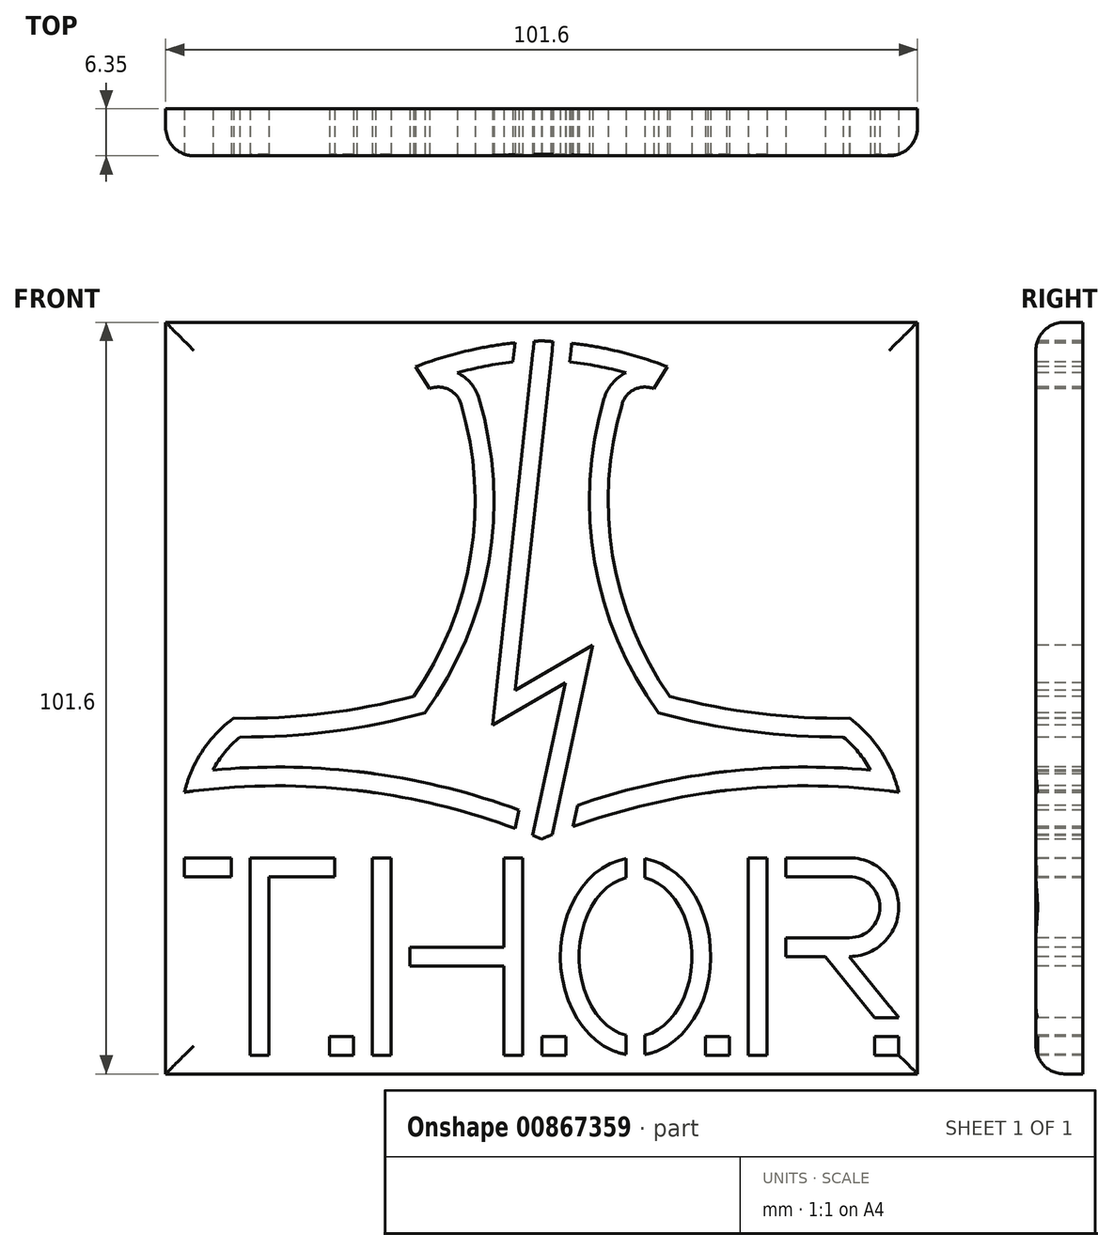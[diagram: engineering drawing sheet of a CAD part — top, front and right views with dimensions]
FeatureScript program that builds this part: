
annotation { "Feature Type Name" : "Feature", "Feature Type Description" : "" }
export const myFeature = defineFeature(function(context is Context, id is Id, definition is map)
    precondition{}
    {
        {
            var Q0;
            Q0=qCreatedBy(makeId("Front.planeOp"),FACE);
            var sketch = newSketch(context, id + "F0", { "sketchPlane" : qUnion([Q0])});
            skLineSegment(sketch, "E0.bottom", {"start": v(50.8, 50.8) * mm, "end": v(-50.8, 50.8) * mm});
            skLineSegment(sketch, "E0.top", {"start": v(50.8, -50.8) * mm, "end": v(-50.8, -50.8) * mm});
            skLineSegment(sketch, "E0.left", {"start": v(50.8, 50.8) * mm, "end": v(50.8, -50.8) * mm});
            skLineSegment(sketch, "E0.right", {"start": v(-50.8, 50.8) * mm, "end": v(-50.8, -50.8) * mm});
            skPoint(sketch, "E0.middle", {"position": v(0, 0) * mm});
            skSolve(sketch);
        }
        {
            var Q0;
            Q0 = qSketchRegion(id + "F0", true);
            extrude(context, id + "F1", {"entities" : qUnion([Q0]), "depth" : 6.35 * mm, "offsetDistance" : 25.4 * mm});
        }
        {
            var Q0;
            Q0=makeQuery(id+"F1.opExtrude","CAP_FACE",FACE,{"disambiguationData":[OSD([sQuery(id+"F0.wireOp",EDGE,"E0.bottom"),sQuery(id+"F0.wireOp",EDGE,"E0.top"),sQuery(id+"F0.wireOp",EDGE,"E0.left"),sQuery(id+"F0.wireOp",EDGE,"E0.right")])],"isStart":false});
            var sketch = newSketch(context, id + "F2", { "sketchPlane" : qUnion([Q0])});
            skLineSegment(sketch, "E1", {"start": v(-25.4, 50.8) * mm, "end": v(-25.4, -50.8) * mm, "construction": true});
            skLineSegment(sketch, "E2", {"start": v(0, 50.8) * mm, "end": v(0, -50.8) * mm, "construction": true});
            skLineSegment(sketch, "E3", {"start": v(25.4, 50.8) * mm, "end": v(25.4, -50.8) * mm, "construction": true});
            skLineSegment(sketch, "E4", {"start": v(-50.8, 0) * mm, "end": v(50.8, 0) * mm, "construction": true});
            skLineSegment(sketch, "E5", {"start": v(-50.8, 25.4) * mm, "end": v(50.8, 25.4) * mm, "construction": true});
            skLineSegment(sketch, "E6", {"start": v(-50.8, -21.6) * mm, "end": v(-41.91, -21.6) * mm, "construction": true});
            skLineSegment(sketch, "E7.bottom", {"start": v(-48.26, -21.6) * mm, "end": v(-41.91, -21.6) * mm});
            skLineSegment(sketch, "E7.top", {"start": v(-48.26, -24.13) * mm, "end": v(-41.91, -24.13) * mm});
            skLineSegment(sketch, "E7.left", {"start": v(-48.26, -21.6) * mm, "end": v(-48.26, -24.13) * mm});
            skLineSegment(sketch, "E7.right", {"start": v(-27.94, -21.6) * mm, "end": v(-27.94, -24.13) * mm});
            skLineSegment(sketch, "E8.top", {"start": v(-39.37, -48.26) * mm, "end": v(-36.83, -48.26) * mm});
            skLineSegment(sketch, "E8.left", {"start": v(-39.37, -24.13) * mm, "end": v(-39.37, -48.26) * mm});
            skLineSegment(sketch, "E8.right", {"start": v(-36.83, -24.13) * mm, "end": v(-36.83, -48.26) * mm});
            skLineSegment(sketch, "E9", {"start": v(-38.1, -21.6) * mm, "end": v(-38.1, -50.8) * mm, "construction": true});
            skLineSegment(sketch, "E10.trimOffspring", {"start": v(-36.83, -24.13) * mm, "end": v(-27.94, -24.13) * mm});
            skLineSegment(sketch, "E11.bottom", {"start": v(-22.86, -21.6) * mm, "end": v(-20.32, -21.6) * mm});
            skLineSegment(sketch, "E11.top", {"start": v(-22.86, -48.26) * mm, "end": v(-20.32, -48.26) * mm});
            skLineSegment(sketch, "E11.left", {"start": v(-22.86, -21.6) * mm, "end": v(-22.86, -48.26) * mm});
            skLineSegment(sketch, "E11.right", {"start": v(-20.32, -21.6) * mm, "end": v(-20.32, -33.66) * mm});
            skLineSegment(sketch, "E12.bottom", {"start": v(-5.08, -21.6) * mm, "end": v(-2.54, -21.6) * mm});
            skLineSegment(sketch, "E12.top", {"start": v(-5.08, -48.26) * mm, "end": v(-2.54, -48.26) * mm});
            skLineSegment(sketch, "E12.left", {"start": v(-5.08, -21.6) * mm, "end": v(-5.08, -33.66) * mm});
            skLineSegment(sketch, "E12.right", {"start": v(-2.54, -21.59) * mm, "end": v(-2.54, -48.26) * mm});
            skLineSegment(sketch, "E13.bottom", {"start": v(-17.78, -33.66) * mm, "end": v(-5.08, -33.66) * mm});
            skLineSegment(sketch, "E13.top", {"start": v(-17.78, -36.2) * mm, "end": v(-5.08, -36.2) * mm});
            skLineSegment(sketch, "E14", {"start": v(-22.86, -34.93) * mm, "end": v(-2.54, -34.93) * mm, "construction": true});
            skLineSegment(sketch, "E15.trimOffspring", {"start": v(-20.32, -36.2) * mm, "end": v(-20.32, -48.26) * mm});
            skLineSegment(sketch, "E16.trimOffspring", {"start": v(-5.08, -36.2) * mm, "end": v(-5.08, -48.26) * mm});
            skLineSegment(sketch, "E17", {"start": v(-2.54, -34.93) * mm, "end": v(25.4, -34.93) * mm, "construction": true});
            skLineSegment(sketch, "E18", {"start": v(12.7, -50.8) * mm, "end": v(12.7, -21.6) * mm, "construction": true});
            skLineSegment(sketch, "E19", {"start": v(2.54, -21.6) * mm, "end": v(2.54, -50.8) * mm, "construction": true});
            skEllipticalArc(sketch, "E20", {});
            skLineSegment(sketch, "E21", {"start": v(-2.54, -48.26) * mm, "end": v(25.4, -48.26) * mm, "construction": true});
            skLineSegment(sketch, "E22", {"start": v(22.86, -48.26) * mm, "end": v(22.86, -21.6) * mm, "construction": true});
            skEllipticalArc(sketch, "E23", {});
            skLineSegment(sketch, "E24.bottom", {"start": v(27.94, -21.59) * mm, "end": v(30.48, -21.59) * mm});
            skLineSegment(sketch, "E24.top", {"start": v(27.94, -48.26) * mm, "end": v(30.48, -48.26) * mm});
            skLineSegment(sketch, "E24.left", {"start": v(27.94, -21.59) * mm, "end": v(27.94, -48.26) * mm});
            skLineSegment(sketch, "E24.right", {"start": v(30.48, -24.13) * mm, "end": v(30.48, -32.39) * mm});
            skArc(sketch, "E25", {"start": v(41.6, -34.93) * mm, "mid": v(48.26, -28.26) * mm, "end": v(41.6, -21.59) * mm});
            skLineSegment(sketch, "E26", {"start": v(48.26, -21.59) * mm, "end": v(48.26, -50.8) * mm, "construction": true});
            skLineSegment(sketch, "E27", {"start": v(25.4, -34.93) * mm, "end": v(30.48, -34.93) * mm, "construction": true});
            skLineSegment(sketch, "E28.bottom", {"start": v(33.02, -21.59) * mm, "end": v(41.6, -21.59) * mm});
            skLineSegment(sketch, "E28.top", {"start": v(33.02, -24.13) * mm, "end": v(41.6, -24.13) * mm});
            skLineSegment(sketch, "E29.bottom", {"start": v(33.02, -34.93) * mm, "end": v(38.33, -34.93) * mm});
            skLineSegment(sketch, "E29.top", {"start": v(33.02, -32.39) * mm, "end": v(41.6, -32.39) * mm});
            skArc(sketch, "E30", {"start": v(41.6, -32.39) * mm, "mid": v(45.72, -28.26) * mm, "end": v(41.6, -24.13) * mm});
            skLineSegment(sketch, "E31.trimOffspring", {"start": v(30.48, -34.93) * mm, "end": v(30.48, -48.26) * mm});
            skLineSegment(sketch, "E32.trimOffspring", {"start": v(41.6, -34.93) * mm, "end": v(48.26, -34.93) * mm, "construction": true});
            skArc(sketch, "E33", {"start": v(48.26, -12.72) * mm, "mid": v(36.62, -11.86) * mm, "end": v(24.97, -12.49) * mm});
            skArc(sketch, "E34", {"start": v(10.88, 39.75) * mm, "mid": v(9.58, 19.25) * mm, "end": v(17.31, 0.22) * mm});
            skArc(sketch, "E35", {"start": v(15.16, 41.8) * mm, "mid": v(12.56, 41.73) * mm, "end": v(10.88, 39.75) * mm});
            skLineSegment(sketch, "E36", {"start": v(15.16, 41.8) * mm, "end": v(17, 44.79) * mm});
            skArc(sketch, "E37", {"start": v(48.26, -12.72) * mm, "mid": v(45.83, -7.14) * mm, "end": v(41.63, -2.72) * mm});
            skArc(sketch, "E38", {"start": v(17.31, 0.22) * mm, "mid": v(29.37, -2.07) * mm, "end": v(41.63, -2.72) * mm});
            skArc(sketch, "E39", {"start": v(17, 44.79) * mm, "mid": v(9.27, 47.12) * mm, "end": v(1.27, 48.2) * mm});
            skArc(sketch, "E40.MirrorCS", {"start": v(-48.26, -12.72) * mm, "mid": v(-36.62, -11.86) * mm, "end": v(-24.97, -12.49) * mm});
            skArc(sketch, "E41.MirrorCS", {"start": v(-48.26, -12.72) * mm, "mid": v(-45.83, -7.14) * mm, "end": v(-41.63, -2.72) * mm});
            skArc(sketch, "E42.MirrorCS", {"start": v(-17.31, 0.22) * mm, "mid": v(-29.37, -2.07) * mm, "end": v(-41.63, -2.72) * mm});
            skArc(sketch, "E43.MirrorCS", {"start": v(-10.88, 39.75) * mm, "mid": v(-9.58, 19.25) * mm, "end": v(-17.31, 0.22) * mm});
            skArc(sketch, "E44.MirrorCS", {"start": v(-15.16, 41.8) * mm, "mid": v(-12.56, 41.73) * mm, "end": v(-10.88, 39.75) * mm});
            skLineSegment(sketch, "E45.MirrorCS", {"start": v(-15.16, 41.8) * mm, "end": v(-17, 44.79) * mm});
            skArc(sketch, "E46.MirrorCS", {"start": v(-17, 44.79) * mm, "mid": v(-9.27, 47.12) * mm, "end": v(-1.27, 48.2) * mm});
            skLineSegment(sketch, "E47", {"start": v(11.43, -24.28) * mm, "end": v(11.43, -21.7) * mm});
            skLineSegment(sketch, "E48", {"start": v(13.97, -24.28) * mm, "end": v(13.97, -21.7) * mm});
            skLineSegment(sketch, "E49", {"start": v(11.43, -48.16) * mm, "end": v(11.43, -45.57) * mm});
            skLineSegment(sketch, "E50", {"start": v(13.97, -45.57) * mm, "end": v(13.97, -48.16) * mm});
            skEllipticalArc(sketch, "E51.trimOffspring", {});
            skEllipticalArc(sketch, "E52.trimOffspring", {});
            skLineSegment(sketch, "E53", {"start": v(30.48, -34.93) * mm, "end": v(30.48, -32.39) * mm});
            skLineSegment(sketch, "E54", {"start": v(33.02, -32.39) * mm, "end": v(33.02, -34.93) * mm});
            skLineSegment(sketch, "E55.trimOffspring", {"start": v(33.02, -34.93) * mm, "end": v(38.33, -34.93) * mm, "construction": true});
            skLineSegment(sketch, "E56", {"start": v(30.48, -24.13) * mm, "end": v(30.48, -21.59) * mm});
            skLineSegment(sketch, "E57", {"start": v(33.02, -21.59) * mm, "end": v(33.02, -24.13) * mm});
            skLineSegment(sketch, "E58.trimOffspring", {"start": v(33.02, -21.59) * mm, "end": v(50.8, -21.59) * mm, "construction": true});
            skLineSegment(sketch, "E59", {"start": v(-20.32, -33.66) * mm, "end": v(-20.32, -36.2) * mm});
            skLineSegment(sketch, "E60", {"start": v(-17.78, -33.66) * mm, "end": v(-17.78, -36.2) * mm});
            skLineSegment(sketch, "E61", {"start": v(-39.37, -24.13) * mm, "end": v(-39.37, -21.6) * mm});
            skLineSegment(sketch, "E62", {"start": v(-41.91, -21.6) * mm, "end": v(-41.91, -24.13) * mm});
            skLineSegment(sketch, "E63.trimOffspring", {"start": v(-39.37, -21.6) * mm, "end": v(30.48, -21.59) * mm, "construction": true});
            skLineSegment(sketch, "E64.trimOffspring", {"start": v(-39.37, -21.6) * mm, "end": v(-27.94, -21.6) * mm});
            skLineSegment(sketch, "E65.bottom", {"start": v(48.26, -48.26) * mm, "end": v(45, -48.26) * mm});
            skLineSegment(sketch, "E65.top", {"start": v(48.26, -45.72) * mm, "end": v(45, -45.72) * mm});
            skLineSegment(sketch, "E65.left", {"start": v(48.26, -48.26) * mm, "end": v(48.26, -45.72) * mm});
            skLineSegment(sketch, "E65.right", {"start": v(45, -48.26) * mm, "end": v(45, -45.72) * mm});
            skLineSegment(sketch, "E66.bottom", {"start": v(25.4, -48.26) * mm, "end": v(22.12, -48.26) * mm});
            skLineSegment(sketch, "E66.top", {"start": v(25.4, -45.72) * mm, "end": v(22.12, -45.72) * mm});
            skLineSegment(sketch, "E66.left", {"start": v(25.4, -48.26) * mm, "end": v(25.4, -45.72) * mm});
            skLineSegment(sketch, "E66.right", {"start": v(22.12, -48.26) * mm, "end": v(22.12, -45.72) * mm});
            skLineSegment(sketch, "E67.bottom", {"start": v(-25.4, -48.26) * mm, "end": v(-28.68, -48.26) * mm});
            skLineSegment(sketch, "E67.top", {"start": v(-25.4, -45.72) * mm, "end": v(-28.68, -45.72) * mm});
            skLineSegment(sketch, "E67.left", {"start": v(-25.4, -48.26) * mm, "end": v(-25.4, -45.72) * mm});
            skLineSegment(sketch, "E67.right", {"start": v(-28.68, -48.26) * mm, "end": v(-28.68, -45.72) * mm});
            skLineSegment(sketch, "E68.bottom", {"start": v(0.02, -48.26) * mm, "end": v(3.3, -48.26) * mm});
            skLineSegment(sketch, "E68.top", {"start": v(0.02, -45.72) * mm, "end": v(3.3, -45.72) * mm});
            skLineSegment(sketch, "E68.left", {"start": v(0.02, -48.26) * mm, "end": v(0.02, -45.72) * mm});
            skLineSegment(sketch, "E68.right", {"start": v(3.3, -48.26) * mm, "end": v(3.3, -45.72) * mm});
            skLineSegment(sketch, "E69", {"start": v(38.33, -34.93) * mm, "end": v(45, -43.18) * mm});
            skLineSegment(sketch, "E70", {"start": v(45, -43.18) * mm, "end": v(48.26, -43.18) * mm});
            skLineSegment(sketch, "E71", {"start": v(48.26, -43.18) * mm, "end": v(41.6, -34.93) * mm});
            skArc(sketch, "E72.0", {"start": v(44.42, -9.72) * mm, "mid": v(34.7, -9.33) * mm, "end": v(24.97, -9.93) * mm});
            skArc(sketch, "E72.1", {"start": v(11.39, 43.98) * mm, "mid": v(6.37, 45.09) * mm, "end": v(1.27, 45.66) * mm});
            skArc(sketch, "E72.2", {"start": v(11.39, 43.98) * mm, "mid": v(9.55, 42.53) * mm, "end": v(8.45, 40.47) * mm});
            skArc(sketch, "E72.3", {"start": v(8.45, 40.47) * mm, "mid": v(7.15, 18.38) * mm, "end": v(15.78, -2) * mm});
            skArc(sketch, "E72.4", {"start": v(15.78, -2) * mm, "mid": v(28.16, -4.47) * mm, "end": v(40.77, -5.27) * mm});
            skArc(sketch, "E72.5", {"start": v(-11.39, 43.98) * mm, "mid": v(-6.37, 45.09) * mm, "end": v(-1.27, 45.66) * mm});
            skArc(sketch, "E72.6", {"start": v(44.42, -9.72) * mm, "mid": v(42.8, -7.32) * mm, "end": v(40.77, -5.27) * mm});
            skArc(sketch, "E72.7", {"start": v(-11.39, 43.98) * mm, "mid": v(-9.55, 42.53) * mm, "end": v(-8.45, 40.47) * mm});
            skArc(sketch, "E72.8", {"start": v(-8.45, 40.47) * mm, "mid": v(-7.15, 18.38) * mm, "end": v(-15.78, -2) * mm});
            skArc(sketch, "E72.9", {"start": v(-15.78, -2) * mm, "mid": v(-28.16, -4.47) * mm, "end": v(-40.77, -5.27) * mm});
            skArc(sketch, "E72.10", {"start": v(-44.42, -9.72) * mm, "mid": v(-42.8, -7.32) * mm, "end": v(-40.77, -5.27) * mm});
            skArc(sketch, "E72.11", {"start": v(-44.42, -9.72) * mm, "mid": v(-34.7, -9.33) * mm, "end": v(-24.97, -9.93) * mm});
            skPoint(sketch, "E73.orphan", {"position": v(0, 48.26) * mm});
            skArc(sketch, "E74.trimOffspring", {"start": v(-22.43, -10.25) * mm, "mid": v(-11.03, -12.59) * mm, "end": v(0, -16.3) * mm});
            skArc(sketch, "E75.trimOffspring", {"start": v(-22.43, -12.82) * mm, "mid": v(-11.02, -15.22) * mm, "end": v(0, -19.05) * mm});
            skArc(sketch, "E76.trimOffspring", {"start": v(22.43, -12.82) * mm, "mid": v(11.02, -15.22) * mm, "end": v(0, -19.05) * mm});
            skArc(sketch, "E77.trimOffspring", {"start": v(22.43, -10.25) * mm, "mid": v(11.03, -12.59) * mm, "end": v(0, -16.3) * mm});
            skArc(sketch, "E78", {"start": v(1.27, 45.66) * mm, "mid": v(0, 45.7) * mm, "end": v(-1.27, 45.66) * mm});
            skArc(sketch, "E79", {"start": v(1.27, 48.2) * mm, "mid": v(0, 48.27) * mm, "end": v(-1.27, 48.2) * mm});
            skArc(sketch, "E80", {"start": v(-22.43, -12.82) * mm, "mid": v(-23.7, -12.62) * mm, "end": v(-24.97, -12.49) * mm});
            skArc(sketch, "E81", {"start": v(-22.43, -10.25) * mm, "mid": v(-23.7, -10.07) * mm, "end": v(-24.97, -9.93) * mm});
            skArc(sketch, "E82.MirrorCS", {"start": v(22.43, -10.25) * mm, "mid": v(23.7, -10.07) * mm, "end": v(24.97, -9.93) * mm});
            skArc(sketch, "E83.MirrorCS", {"start": v(22.43, -12.82) * mm, "mid": v(23.7, -12.62) * mm, "end": v(24.97, -12.49) * mm});
            const initialGuessF2  = {"E20": [0.0127, -0.034925, 0, 1, 0.013335, 0.01016, 0.12532783116806362, 3.016264822421728], "E23": [0.0127, -0.034925, 0, 1, 0.010795, 0.00762, 0.167448079219667, 2.9741445743701163], "E51.trimOffspring": [0.0127, -0.034925, 0, 1, 0.010795, 0.00762, 3.3090407328094815, 6.115737227959899], "E52.trimOffspring": [0.0127, -0.034925, 0, 1, 0.013335, 0.01016, 3.2669204847578577, 6.157857476011521]};
            skSetInitialGuess(sketch, initialGuessF2);
            skSolve(sketch);
        }
        {
            var Q0;
            Q0 = qSketchRegion(id + "F2", true);
            extrude(context, id + "F3", {"entities" : qUnion([Q0]), "operationType" : NewBodyOperationType.REMOVE, "oppositeDirection" : true, "depth" : 25.4 * mm, "offsetDistance" : 25.4 * mm});
        }
        {
            var Q0;
            Q0=makeQuery(id+"F1.opExtrude","CAP_FACE",FACE,{"disambiguationData":[OSD([sQuery(id+"F0.wireOp",EDGE,"E0.bottom"),sQuery(id+"F0.wireOp",EDGE,"E0.top"),sQuery(id+"F0.wireOp",EDGE,"E0.left"),sQuery(id+"F0.wireOp",EDGE,"E0.right")])],"isStart":false});
            var sketch = newSketch(context, id + "F4", { "sketchPlane" : qUnion([Q0])});
            skLineSegment(sketch, "E84", {"start": v(0, -19.05) * mm, "end": v(5.08, 4.6) * mm, "construction": true});
            skLineSegment(sketch, "E85", {"start": v(5.08, 4.6) * mm, "end": v(-5.08, -1.3) * mm, "construction": true});
            skLineSegment(sketch, "E86", {"start": v(-5.08, -1.3) * mm, "end": v(0, 45.7) * mm, "construction": true});
            skLineSegment(sketch, "E87", {"start": v(0, 45.7) * mm, "end": v(0, -19.05) * mm, "construction": true});
            skLineSegment(sketch, "E88.0", {"start": v(-3.55, 1.06) * mm, "end": v(1.26, 45.57) * mm});
            skLineSegment(sketch, "E88.1", {"start": v(6.92, 7.14) * mm, "end": v(-3.55, 1.06) * mm});
            skLineSegment(sketch, "E88.2", {"start": v(1.71, -17.13) * mm, "end": v(6.92, 7.14) * mm});
            skLineSegment(sketch, "E89.0", {"start": v(-6.61, -3.66) * mm, "end": v(-1.26, 45.84) * mm});
            skLineSegment(sketch, "E89.1", {"start": v(3.24, 2.06) * mm, "end": v(-6.61, -3.66) * mm});
            skLineSegment(sketch, "E89.2", {"start": v(-0.76, -16.53) * mm, "end": v(3.24, 2.06) * mm});
            skLineSegment(sketch, "E90", {"start": v(-0.76, -16.53) * mm, "end": v(1.71, -17.13) * mm});
            skLineSegment(sketch, "E91", {"start": v(1.26, 45.57) * mm, "end": v(1.36, 46.43) * mm});
            skLineSegment(sketch, "E92", {"start": v(1.36, 46.43) * mm, "end": v(-1.26, 45.84) * mm});
            skSolve(sketch);
        }
        {
            var Q0;
            Q0 = qSketchRegion(id + "F4", true);
            extrude(context, id + "F5", {"entities" : qUnion([Q0]), "operationType" : NewBodyOperationType.REMOVE, "oppositeDirection" : true, "depth" : 25.4 * mm, "offsetDistance" : 25.4 * mm});
        }
        {
            var Q0;
            Q0=makeQuery(id+"F1.opExtrude","CAP_FACE",FACE,{"disambiguationData":[OSD([sQuery(id+"F0.wireOp",EDGE,"E0.bottom"),sQuery(id+"F0.wireOp",EDGE,"E0.top"),sQuery(id+"F0.wireOp",EDGE,"E0.left"),sQuery(id+"F0.wireOp",EDGE,"E0.right")])],"isStart":false});
            var sketch = newSketch(context, id + "F6", { "sketchPlane" : qUnion([Q0])});
            skLineSegment(sketch, "E93", {"start": v(-1.28, 45.66) * mm, "end": v(-0.95, 48.7) * mm});
            skLineSegment(sketch, "E94", {"start": v(-0.95, 48.7) * mm, "end": v(-3.48, 48.97) * mm});
            skLineSegment(sketch, "E95", {"start": v(-3.48, 48.97) * mm, "end": v(-3.97, 44.4) * mm});
            skLineSegment(sketch, "E96", {"start": v(-3.97, 44.4) * mm, "end": v(-1.28, 45.66) * mm});
            skLineSegment(sketch, "E97", {"start": v(1.27, 45.66) * mm, "end": v(1.69, 49.5) * mm});
            skLineSegment(sketch, "E98", {"start": v(1.69, 49.5) * mm, "end": v(4.21, 49.24) * mm});
            skLineSegment(sketch, "E99", {"start": v(4.21, 49.24) * mm, "end": v(3.73, 44.79) * mm});
            skLineSegment(sketch, "E100", {"start": v(3.73, 44.79) * mm, "end": v(1.27, 45.66) * mm});
            skLineSegment(sketch, "E101", {"start": v(-0.38, -14.76) * mm, "end": v(-1.46, -19.82) * mm});
            skLineSegment(sketch, "E102", {"start": v(-1.46, -19.82) * mm, "end": v(-3.87, -18.91) * mm});
            skLineSegment(sketch, "E103", {"start": v(-3.87, -18.91) * mm, "end": v(-2.67, -13.32) * mm});
            skLineSegment(sketch, "E104", {"start": v(-2.67, -13.32) * mm, "end": v(-0.38, -14.76) * mm});
            skLineSegment(sketch, "E105", {"start": v(2.22, -14.76) * mm, "end": v(1.02, -20.33) * mm});
            skLineSegment(sketch, "E106", {"start": v(1.02, -20.33) * mm, "end": v(3.62, -20.33) * mm});
            skLineSegment(sketch, "E107", {"start": v(3.62, -20.33) * mm, "end": v(5.1, -13.46) * mm});
            skLineSegment(sketch, "E108", {"start": v(5.1, -13.46) * mm, "end": v(2.22, -14.76) * mm});
            skSolve(sketch);
        }
        {
            var Q0;
            Q0 = qSketchRegion(id + "F6", true);
            extrude(context, id + "F7", {"entities" : qUnion([Q0]), "operationType" : NewBodyOperationType.ADD, "oppositeDirection" : true, "depth" : 6.35 * mm, "offsetDistance" : 25.4 * mm});
        }
        {
            var Q0;
            Q0=makeQuery(id+"F1.opExtrude","CAP_EDGE",EDGE,{"disambiguationData":[OSD([sQuery(id+"F0.wireOp",EDGE,"E0.left")])],"isStart":false});
            var Q1;
            Q1=makeQuery(id+"F1.opExtrude","CAP_EDGE",EDGE,{"disambiguationData":[OSD([sQuery(id+"F0.wireOp",EDGE,"E0.top")])],"isStart":false});
            var Q2;
            Q2=makeQuery(id+"F1.opExtrude","CAP_EDGE",EDGE,{"disambiguationData":[OSD([sQuery(id+"F0.wireOp",EDGE,"E0.bottom")])],"isStart":false});
            var Q3;
            Q3=makeQuery(id+"F1.opExtrude","CAP_EDGE",EDGE,{"disambiguationData":[OSD([sQuery(id+"F0.wireOp",EDGE,"E0.right")])],"isStart":false});
            fillet(context, id + "F8", {"entities" : qUnion([Q0, Q1, Q2, Q3]), "radius" : 3.8 * mm, "tangentPropagation" : true, "allowEdgeOverflow" : false});
        }
    });
